# Revit family: Vistafold_Sliding_Folding_5_Custom
name_source: partatom
category: Doors
revit_build: Autodesk Revit 2014 (Build: 20130308_1515(x64)
units: mm (PartAtom-declared; Revit-internal decimal feet)

## types (1)
- Vistafold-5-Custom
    All Available Glazing Numbers = The rows below list the available glazing materials for this window:
    Centered In Wall = Yes
    Custom Door Height = 2090 mm  [stored 6.85696 ft]
    Custom Door Width = 1790 mm  [stored 5.8727 ft]
    Custom Frame Offset From Exterior = 0 mm  [stored 0 ft]
    Custom Windload = 1000 mm  [stored 3.28084 ft]
    DG Air Gap Thickness = 12 mm  [stored 0.0393701 ft]
    DG Thickness Calc = 6 mm  [stored 0.019685 ft]
    Default Sill Height = 0 mm  [stored 0 ft]
    Description = Sliding folding door, 5 panel custom
    Double Glazing Gasket Material = Double Glazing Gasket Material
    Frame Thickness = 75 mm  [stored 0.246063 ft]
    Height = 2090 mm  [stored 6.85696 ft]
    IGDB or SAGDB Number = 0
    Limit Door Height Max = 2467 mm  [stored 8.09383 ft]
    Limit Door Height Min = 367 mm  [stored 1.20407 ft]
    Limit Door Width Max = 4584 mm
    Limit Door Width Min = 1584 mm  [stored 5.19685 ft]
    Limit Sash Height Max = 2400 mm
    Limit Sash Height Min = 300 mm  [stored 0.984252 ft]
    Limit Sash Width Max = 900 mm  [stored 2.95276 ft]
    Limit Sash Width Min = 300 mm  [stored 0.984252 ft]
    Manufacturer = Crealco
    Max Pane Area = 0.51 m²
    Max System DG One Piece Thickness = 6 mm  [stored 0.019685 ft]
    Max System DG Unit Thickness = 25 mm  [stored 0.082021 ft]
    Model = Vistafold
    Number Of Sash Inserts = 5
    Rough Width = 3 mm  [stored 0.00984252 ft]
    Sash Bottom Gap = 33 mm  [stored 0.108268 ft]
    Sash Frame Seal = 3 mm  [stored 0.00984252 ft]
    Sash Height = 2023 mm  [stored 6.63714 ft]
    Sash Side Gap = 34 mm  [stored 0.111549 ft]
    Sash Spacing Gap = 4 mm  [stored 0.0131234 ft]
    Sash Top Gap = 34 mm  [stored 0.111549 ft]
    Sash Width = 341 mm
    Thickness = 758 mm
    URL = http://www.crealco.co.za
    Wall Closure = By host
    Width = 1790 mm  [stored 5.8727 ft]
    Windload Design = 1000 mm  [stored 3.28084 ft]

note: [stored X ft] marks values corroborated as IEEE doubles in the binary element streams (Revit-internal decimal feet)

## geometry (parser evidence)
native form markers: Sweep x28
no freeform markers — native parametric forms only
